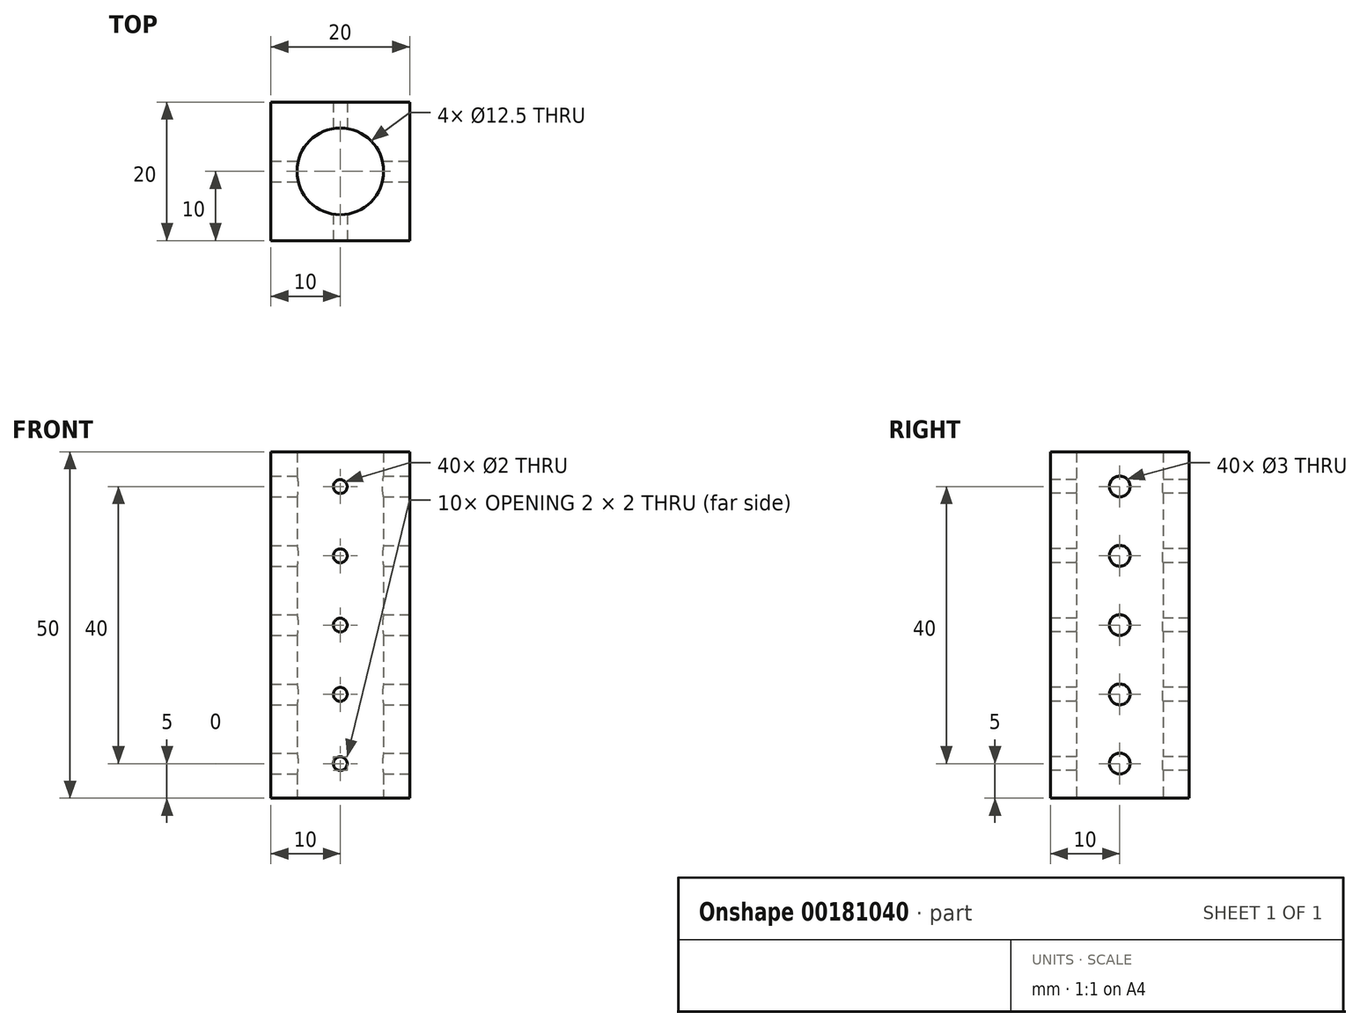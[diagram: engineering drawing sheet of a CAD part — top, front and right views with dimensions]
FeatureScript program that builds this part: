
annotation { "Feature Type Name" : "Feature", "Feature Type Description" : "" }
export const myFeature = defineFeature(function(context is Context, id is Id, definition is map)
    precondition{}
    {
        {
            var Q0;
            Q0=qCreatedBy(makeId("Top.planeOp"),FACE);
            var sketch = newSketch(context, id + "F0", { "sketchPlane" : qUnion([Q0])});
            skCircle(sketch, "E0", {"center": v(0, 0) * mm, "radius": 6.25 * mm});
            skLineSegment(sketch, "E1.bottom", {"start": v(-10, -10) * mm, "end": v(10, -10) * mm});
            skLineSegment(sketch, "E1.top", {"start": v(-10, 10) * mm, "end": v(10, 10) * mm});
            skLineSegment(sketch, "E1.left", {"start": v(-10, -10) * mm, "end": v(-10, 10) * mm});
            skLineSegment(sketch, "E1.right", {"start": v(10, -10) * mm, "end": v(10, 10) * mm});
            skSolve(sketch);
        }
        {
            var Q0;
            Q0=makeQuery(id+"F0.imprint","IMPRINT",FACE,{"disambiguationData":[TD([[makeQuery(id+"F0.imprint","IMPRINT",EDGE,{"derivedFrom":sQuery(id+"F0.wireOp",EDGE,"E0")}),-1.0]])]});
            extrude(context, id + "F1", {"entities" : qUnion([Q0]), "depth" : 50 * mm});
        }
        {
            var Q0;
            Q0=makeQuery(id+"F1.opExtrude","SWEPT_FACE",FACE,{"disambiguationData":[OSD([sQuery(id+"F0.wireOp",EDGE,"E1.right")])]});
            var sketch = newSketch(context, id + "F2", { "sketchPlane" : qUnion([Q0])});
            skCircle(sketch, "E2", {"center": v(0, 45) * mm, "radius": 1.5 * mm});
            skPoint(sketch, "E2.centerSnap0", {"position": v(0, 50) * mm});
            skCircle(sketch, "E3", {"center": v(0, 35) * mm, "radius": 1.5 * mm});
            skCircle(sketch, "E4", {"center": v(0, 25) * mm, "radius": 1.5 * mm});
            skCircle(sketch, "E5", {"center": v(0, 5) * mm, "radius": 1.5 * mm});
            skCircle(sketch, "E6", {"center": v(0, 15) * mm, "radius": 1.5 * mm});
            skSolve(sketch);
        }
        {
            var Q0;
            Q0=makeQuery(id+"F2.imprint","IMPRINT",FACE,{"disambiguationData":[TD([[makeQuery(id+"F2.imprint","IMPRINT",EDGE,{"derivedFrom":sQuery(id+"F2.wireOp",EDGE,"E2")}),1.0]])]});
            var Q1;
            Q1=makeQuery(id+"F2.imprint","IMPRINT",FACE,{"disambiguationData":[TD([[makeQuery(id+"F2.imprint","IMPRINT",EDGE,{"derivedFrom":sQuery(id+"F2.wireOp",EDGE,"E3")}),1.0]])]});
            var Q2;
            Q2=makeQuery(id+"F2.imprint","IMPRINT",FACE,{"disambiguationData":[TD([[makeQuery(id+"F2.imprint","IMPRINT",EDGE,{"derivedFrom":sQuery(id+"F2.wireOp",EDGE,"E4")}),1.0]])]});
            var Q3;
            Q3=makeQuery(id+"F2.imprint","IMPRINT",FACE,{"disambiguationData":[TD([[makeQuery(id+"F2.imprint","IMPRINT",EDGE,{"derivedFrom":sQuery(id+"F2.wireOp",EDGE,"E6")}),1.0]])]});
            var Q4;
            Q4=makeQuery(id+"F2.imprint","IMPRINT",FACE,{"disambiguationData":[TD([[makeQuery(id+"F2.imprint","IMPRINT",EDGE,{"derivedFrom":sQuery(id+"F2.wireOp",EDGE,"E5")}),1.0]])]});
            var Q5;
            Q5=makeQuery(id+"F1.opExtrude","SWEPT_FACE",FACE,{"disambiguationData":[OSD([sQuery(id+"F0.wireOp",EDGE,"E1.left")])]});
            extrude(context, id + "F3", {"entities" : qUnion([Q0, Q1, Q2, Q3, Q4]), "operationType" : NewBodyOperationType.REMOVE, "endBound" : BoundingType.UP_TO_SURFACE, "oppositeDirection" : true, "endBoundEntityFace" : qUnion([Q5]), "depth" : 25 * mm});
        }
        {
            var Q0;
            Q0=makeQuery(id+"F1.opExtrude","SWEPT_FACE",FACE,{"disambiguationData":[OSD([sQuery(id+"F0.wireOp",EDGE,"E1.bottom")])]});
            var sketch = newSketch(context, id + "F4", { "sketchPlane" : qUnion([Q0])});
            skCircle(sketch, "E7", {"center": v(0, 45) * mm, "radius": 1 * mm});
            skPoint(sketch, "E7.centerSnap0", {"position": v(0, 50) * mm});
            skCircle(sketch, "E8", {"center": v(0, 35) * mm, "radius": 1 * mm});
            skCircle(sketch, "E9", {"center": v(0, 25) * mm, "radius": 1 * mm});
            skCircle(sketch, "E10", {"center": v(0, 15) * mm, "radius": 1 * mm});
            skCircle(sketch, "E11", {"center": v(0, 5) * mm, "radius": 1 * mm});
            skSolve(sketch);
        }
        {
            var Q0;
            Q0=makeQuery(id+"F4.imprint","IMPRINT",FACE,{"disambiguationData":[TD([[makeQuery(id+"F4.imprint","IMPRINT",EDGE,{"derivedFrom":sQuery(id+"F4.wireOp",EDGE,"E7")}),1.0]])]});
            var Q1;
            Q1=makeQuery(id+"F4.imprint","IMPRINT",FACE,{"disambiguationData":[TD([[makeQuery(id+"F4.imprint","IMPRINT",EDGE,{"derivedFrom":sQuery(id+"F4.wireOp",EDGE,"E8")}),1.0]])]});
            var Q2;
            Q2=makeQuery(id+"F4.imprint","IMPRINT",FACE,{"disambiguationData":[TD([[makeQuery(id+"F4.imprint","IMPRINT",EDGE,{"derivedFrom":sQuery(id+"F4.wireOp",EDGE,"E9")}),1.0]])]});
            var Q3;
            Q3=makeQuery(id+"F4.imprint","IMPRINT",FACE,{"disambiguationData":[TD([[makeQuery(id+"F4.imprint","IMPRINT",EDGE,{"derivedFrom":sQuery(id+"F4.wireOp",EDGE,"E10")}),1.0]])]});
            var Q4;
            Q4=makeQuery(id+"F4.imprint","IMPRINT",FACE,{"disambiguationData":[TD([[makeQuery(id+"F4.imprint","IMPRINT",EDGE,{"derivedFrom":sQuery(id+"F4.wireOp",EDGE,"E11")}),1.0]])]});
            var Q5;
            Q5=makeQuery(id+"F1.opExtrude","SWEPT_FACE",FACE,{"disambiguationData":[OSD([sQuery(id+"F0.wireOp",EDGE,"E1.top")])]});
            extrude(context, id + "F5", {"entities" : qUnion([Q0, Q1, Q2, Q3, Q4]), "operationType" : NewBodyOperationType.REMOVE, "endBound" : BoundingType.UP_TO_SURFACE, "oppositeDirection" : true, "endBoundEntityFace" : qUnion([Q5]), "depth" : 25 * mm});
        }
    });
